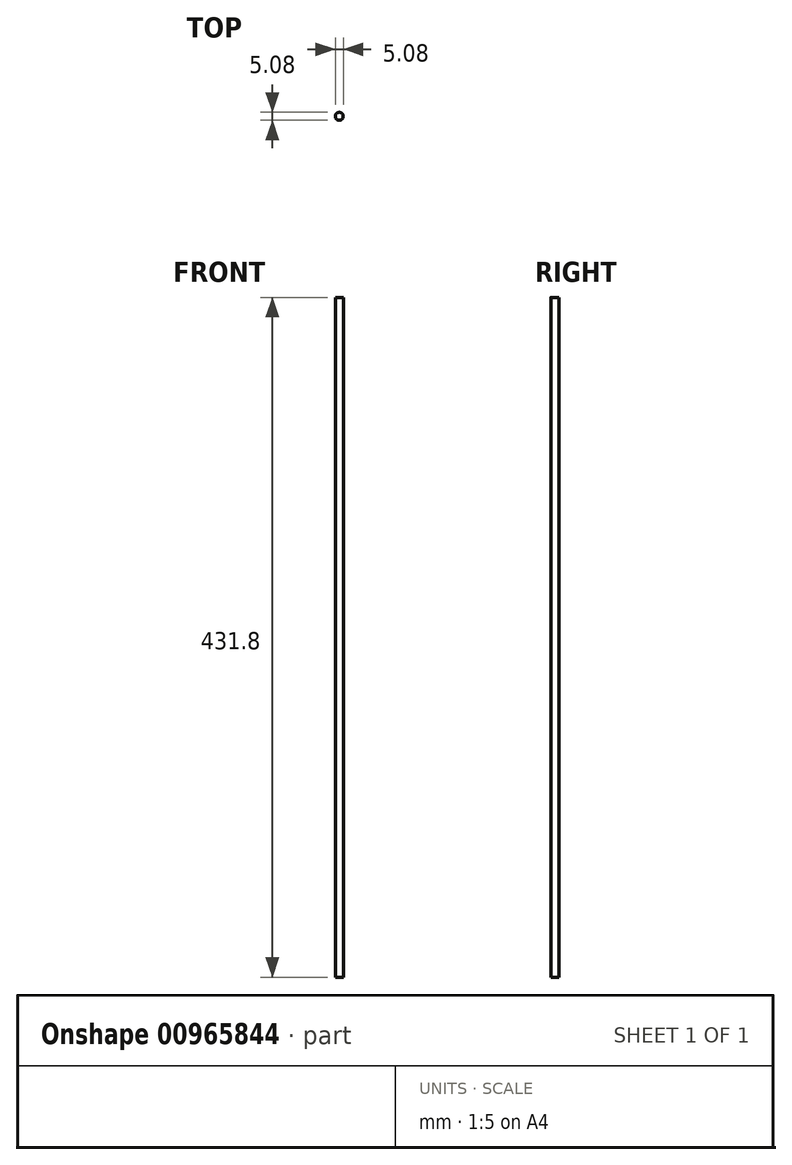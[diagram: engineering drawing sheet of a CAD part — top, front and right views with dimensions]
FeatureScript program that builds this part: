
annotation { "Feature Type Name" : "Feature", "Feature Type Description" : "" }
export const myFeature = defineFeature(function(context is Context, id is Id, definition is map)
    precondition{}
    {
        {
            var Q0;
            Q0=qCreatedBy(makeId("Top.planeOp"),FACE);
            var sketch = newSketch(context, id + "F0", { "sketchPlane" : qUnion([Q0])});
            skCircle(sketch, "E0", {"center": v(0, 0) * mm, "radius": 2.54 * mm});
            skSolve(sketch);
        }
        {
            var Q0;
            Q0 = qSketchRegion(id + "F0", true);
            extrude(context, id + "F1", {"entities" : qUnion([Q0]), "depth" : 431.8 * mm, "offsetDistance" : 25.4 * mm});
        }
    });
